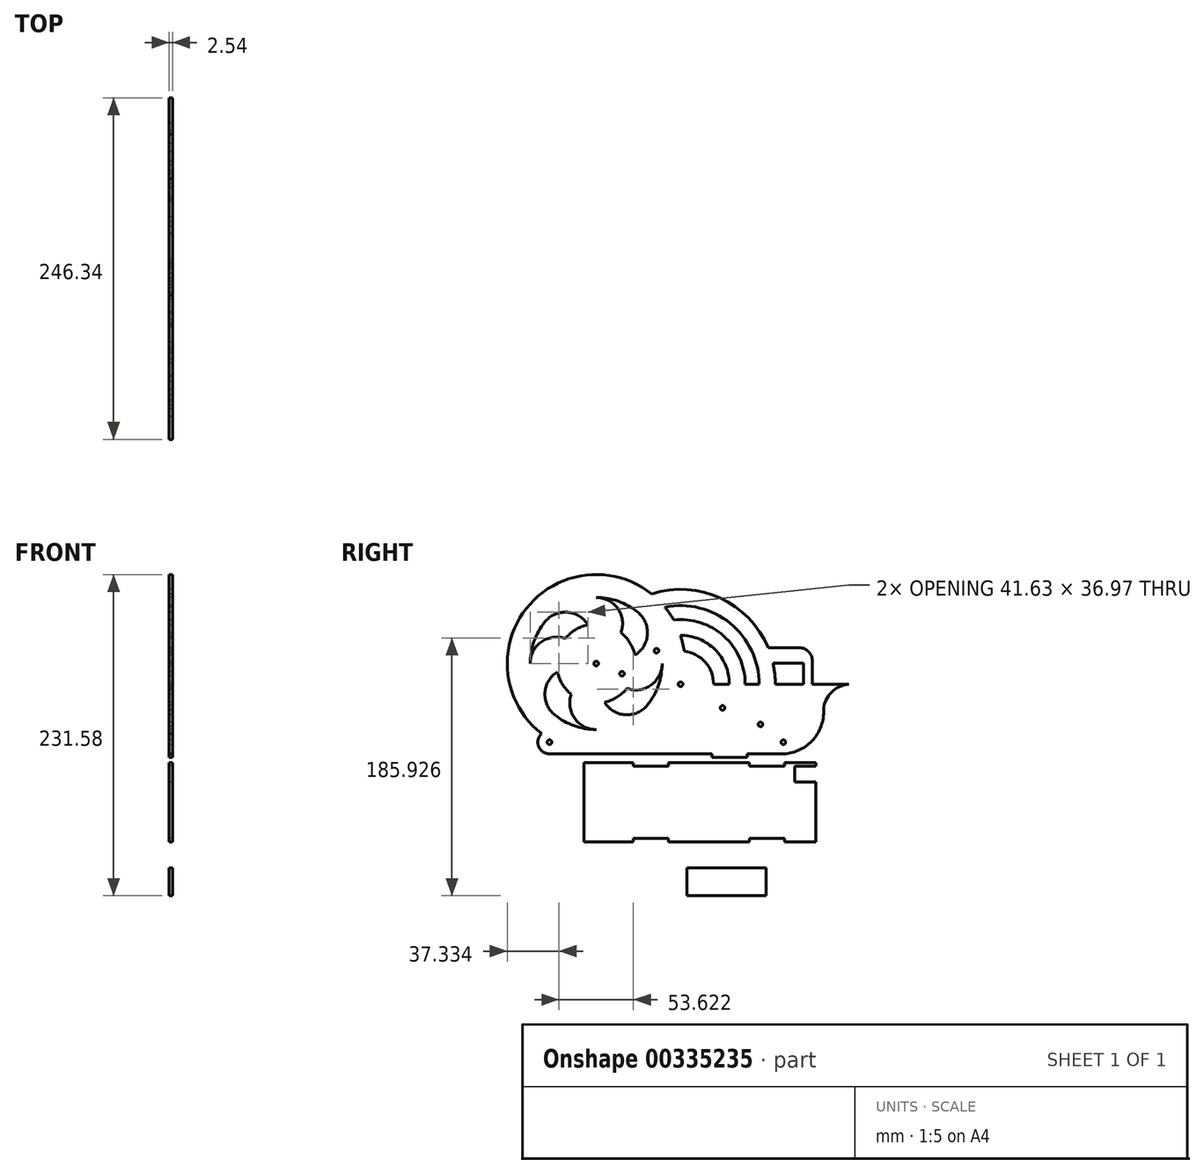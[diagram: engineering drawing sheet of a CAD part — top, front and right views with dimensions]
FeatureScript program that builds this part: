
annotation { "Feature Type Name" : "Feature", "Feature Type Description" : "" }
export const myFeature = defineFeature(function(context is Context, id is Id, definition is map)
    precondition{}
    {
        {
            var Q0;
            Q0=qCreatedBy(makeId("Right.planeOp"),FACE);
            var sketch = newSketch(context, id + "F0", { "sketchPlane" : qUnion([Q0])});
            skLineSegment(sketch, "E0.top", {"start": v(-77.01, -68.22) * mm, "end": v(57.1, -68.22) * mm});
            skArc(sketch, "E1", {"start": v(-113.69, 26.92) * mm, "mid": v(-121.55, 12.87) * mm, "end": v(-124.27, -3) * mm});
            skArc(sketch, "E2", {"start": v(-104.58, -9) * mm, "mid": v(-100.99, -17.98) * mm, "end": v(-94.6, -25.23) * mm});
            skArc(sketch, "E3", {"start": v(-48.7, 2.99) * mm, "mid": v(-39.67, 18) * mm, "end": v(-46.71, 34.03) * mm});
            skArc(sketch, "E4", {"start": v(-82.64, 24.93) * mm, "mid": v(-97.65, 33.96) * mm, "end": v(-113.69, 26.92) * mm});
            skArc(sketch, "E5.trimOffspring", {"start": v(-104.58, -9) * mm, "mid": v(-113.62, -24.01) * mm, "end": v(-106.58, -40.05) * mm});
            skArc(sketch, "E6.trimOffspring", {"start": v(-58.68, 19.22) * mm, "mid": v(-61.1, 36.56) * mm, "end": v(-76.65, 44.62) * mm});
            skArc(sketch, "E7.trimOffspring", {"start": v(-54.42, -20.97) * mm, "mid": v(-37.07, -18.56) * mm, "end": v(-29.02, -3) * mm});
            skArc(sketch, "E8.trimOffspring", {"start": v(-70.65, -30.95) * mm, "mid": v(-55.64, -39.98) * mm, "end": v(-39.6, -32.94) * mm});
            skArc(sketch, "E9.trimOffspring", {"start": v(-94.6, -25.23) * mm, "mid": v(-92.2, -42.58) * mm, "end": v(-76.65, -50.63) * mm});
            skArc(sketch, "E10.trimOffspring", {"start": v(-98.87, 14.95) * mm, "mid": v(-116.22, 12.54) * mm, "end": v(-124.27, -3) * mm});
            skArc(sketch, "E11.trimOffspring", {"start": v(-82.64, 24.93) * mm, "mid": v(-91.61, 21.33) * mm, "end": v(-98.87, 14.95) * mm});
            skArc(sketch, "E12.trimOffspring", {"start": v(-48.7, 2.99) * mm, "mid": v(-52.3, 11.96) * mm, "end": v(-58.68, 19.22) * mm});
            skArc(sketch, "E13.trimOffspring", {"start": v(-70.65, -30.95) * mm, "mid": v(-61.68, -27.35) * mm, "end": v(-54.42, -20.97) * mm});
            skArc(sketch, "E14.trimOffspring", {"start": v(-46.71, 34.03) * mm, "mid": v(-60.77, 41.9) * mm, "end": v(-76.65, 44.62) * mm});
            skArc(sketch, "E15.trimOffspring", {"start": v(-39.6, -32.94) * mm, "mid": v(-31.74, -18.88) * mm, "end": v(-29.02, -3) * mm});
            skArc(sketch, "E16.trimOffspring", {"start": v(-106.58, -40.05) * mm, "mid": v(-92.52, -47.91) * mm, "end": v(-76.65, -50.63) * mm});
            skArc(sketch, "E17", {"start": v(-116.08, -53.6) * mm, "mid": v(-118.2, -62.86) * mm, "end": v(-110.34, -68.22) * mm});
            skLineSegment(sketch, "E18", {"start": v(-77.01, -68.22) * mm, "end": v(-110.34, -68.22) * mm});
            skCircle(sketch, "E19", {"center": v(-76.65, -3) * mm, "radius": 1.65 * mm});
            skCircle(sketch, "E20", {"center": v(-110.34, -59.78) * mm, "radius": 1.65 * mm});
            skCircle(sketch, "E21", {"center": v(-58, -10.34) * mm, "radius": 1.65 * mm});
            skCircle(sketch, "E22", {"center": v(-33.13, 6.22) * mm, "radius": 1.65 * mm});
            skCircle(sketch, "E23", {"center": v(-15.73, -17.93) * mm, "radius": 1.65 * mm});
            skCircle(sketch, "E24", {"center": v(58.48, -59.78) * mm, "radius": 1.65 * mm});
            skLineSegment(sketch, "E25", {"start": v(-110.34, -59.78) * mm, "end": v(124.2, -59.78) * mm, "construction": true});
            skArc(sketch, "E26", {"start": v(105.55, -17.93) * mm, "mid": v(93.18, -23.78) * mm, "end": v(87.46, -36.2) * mm});
            skArc(sketch, "E27.trimOffspring", {"start": v(57.1, -68.22) * mm, "mid": v(79.18, -58.75) * mm, "end": v(87.46, -36.2) * mm});
            skLineSegment(sketch, "E28", {"start": v(105.55, -17.93) * mm, "end": v(79.3, -17.93) * mm});
            skPoint(sketch, "E29.orphan", {"position": v(-6.62, -17.93) * mm});
            skArc(sketch, "E30.trimOffspring", {"start": v(52.65, -17.93) * mm, "mid": v(52.23, -10.34) * mm, "end": v(50.97, -2.85) * mm});
            skLineSegment(sketch, "E31", {"start": v(47.42, 8.3) * mm, "end": v(70.21, 8.3) * mm});
            skLineSegment(sketch, "E32", {"start": v(79.3, -0.8) * mm, "end": v(79.3, -17.93) * mm});
            skLineSegment(sketch, "E33", {"start": v(50.97, -2.85) * mm, "end": v(72.84, -2.85) * mm});
            skLineSegment(sketch, "E34", {"start": v(72.84, -2.85) * mm, "end": v(72.84, -17.93) * mm});
            skArc(sketch, "E35", {"start": v(79.3, -0.8) * mm, "mid": v(76.64, 5.64) * mm, "end": v(70.21, 8.3) * mm});
            skArc(sketch, "E36.trimOffspring", {"start": v(47.42, 8.3) * mm, "mid": v(12.95, 44.14) * mm, "end": v(-36.68, 47.16) * mm});
            skLineSegment(sketch, "E37.trimOffspring", {"start": v(72.84, -17.93) * mm, "end": v(52.65, -17.93) * mm});
            skCircle(sketch, "E38", {"center": v(14.56, -35.01) * mm, "radius": 1.65 * mm});
            skCircle(sketch, "E39", {"center": v(41.94, -46.95) * mm, "radius": 1.65 * mm});
            skArc(sketch, "E40", {"start": v(-13.1, 5.78) * mm, "mid": v(-14.18, 11.58) * mm, "end": v(-15.8, 17.27) * mm});
            skArc(sketch, "E41", {"start": v(8.13, -17.93) * mm, "mid": v(2.04, -2.02) * mm, "end": v(-13.1, 5.78) * mm});
            skLineSegment(sketch, "E42", {"start": v(40.93, -17.93) * mm, "end": v(30.9, -17.93) * mm});
            skArc(sketch, "E43.trimOffspring", {"start": v(40.93, -17.93) * mm, "mid": v(20.13, 25.93) * mm, "end": v(-27, 37.6) * mm});
            skArc(sketch, "E44.trimOffspring", {"start": v(-36.68, 47.16) * mm, "mid": v(-127.02, 36.7) * mm, "end": v(-116.08, -53.6) * mm});
            skArc(sketch, "E45", {"start": v(30.9, -17.93) * mm, "mid": v(15.42, 16.76) * mm, "end": v(-20.73, 28.42) * mm});
            skArc(sketch, "E46", {"start": v(19.47, -17.93) * mm, "mid": v(9.14, 6.98) * mm, "end": v(-15.8, 17.27) * mm});
            skLineSegment(sketch, "E47.trimOffspring", {"start": v(19.47, -17.93) * mm, "end": v(8.13, -17.93) * mm});
            skArc(sketch, "E48.trimOffspring", {"start": v(-20.73, 28.42) * mm, "mid": v(-23.66, 33.14) * mm, "end": v(-27, 37.6) * mm});
            skLineSegment(sketch, "E49.bottom", {"start": v(-77.01, -68.22) * mm, "end": v(-51.61, -68.22) * mm});
            skLineSegment(sketch, "E49.top", {"start": v(-77.01, -70.76) * mm, "end": v(-51.61, -70.76) * mm});
            skLineSegment(sketch, "E49.left", {"start": v(-77.01, -68.22) * mm, "end": v(-77.01, -70.76) * mm});
            skLineSegment(sketch, "E49.right", {"start": v(-51.61, -68.22) * mm, "end": v(-51.61, -70.76) * mm});
            skLineSegment(sketch, "E50.bottom", {"start": v(32.38, -68.22) * mm, "end": v(57.78, -68.22) * mm});
            skLineSegment(sketch, "E51", {"start": v(-110.34, -86.16) * mm, "end": v(57.1, -86.16) * mm, "construction": true});
            skLineSegment(sketch, "E52", {"start": v(-110.34, -77.8) * mm, "end": v(-77.01, -77.8) * mm, "construction": true});
            skLineSegment(sketch, "E53.bottom", {"start": v(6.98, -70.76) * mm, "end": v(32.38, -70.76) * mm});
            skLineSegment(sketch, "E53.top", {"start": v(6.98, -68.22) * mm, "end": v(32.38, -68.22) * mm});
            skLineSegment(sketch, "E53.left", {"start": v(6.98, -70.76) * mm, "end": v(6.98, -68.22) * mm});
            skLineSegment(sketch, "E53.right", {"start": v(32.38, -70.76) * mm, "end": v(32.38, -68.22) * mm});
            skPoint(sketch, "E50.top.start.orphan", {"position": v(23.32, -70.76) * mm});
            skLineSegment(sketch, "E54", {"start": v(6.98, -77.7) * mm, "end": v(-51.61, -77.7) * mm, "construction": true});
            skSolve(sketch);
        }
        {
            var Q0;
            Q0=makeQuery(id+"F0.imprint","IMPRINT",FACE,{"disambiguationData":[TD([[makeQuery(id+"F0.imprint","IMPRINT",EDGE,{"derivedFrom":sQuery(id+"F0.wireOp",EDGE,"E1")}),-1.0]])]});
            var Q1;
            Q1=makeQuery(id+"F0.imprint","IMPRINT",FACE,{"disambiguationData":[TD([[makeQuery(id+"F0.imprint","IMPRINT",EDGE,{"derivedFrom":sQuery(id+"F0.wireOp",EDGE,"E0.right")}),-1.0]])]});
            var Q2;
            Q2=makeQuery(id+"F0.imprint","IMPRINT",FACE,{"disambiguationData":[TD([[makeQuery(id+"F0.imprint","IMPRINT",EDGE,{"derivedFrom":sQuery(id+"F0.wireOp",EDGE,"E49.bottom")}),-1.0]])]});
            var Q3;
            Q3=makeQuery(id+"F0.imprint","IMPRINT",FACE,{"disambiguationData":[TD([[makeQuery(id+"F0.imprint","IMPRINT",EDGE,{"derivedFrom":sQuery(id+"F0.wireOp",EDGE,"E50.bottom")}),-1.0]])]});
            var Q4;
            Q4=makeQuery(id+"F0.imprint","IMPRINT",FACE,{"disambiguationData":[TD([[makeQuery(id+"F0.imprint","IMPRINT",EDGE,{"derivedFrom":sQuery(id+"F0.wireOp",EDGE,"E53.bottom")}),1.0]])]});
            extrude(context, id + "F1", {"entities" : qUnion([Q0, Q1, Q2, Q3, Q4]), "depth" : 2.54 * mm});
        }
        {
            var Q0;
            Q0=qCreatedBy(makeId("Right.planeOp"),FACE);
            var sketch = newSketch(context, id + "F2", { "sketchPlane" : qUnion([Q0])});
            skLineSegment(sketch, "E55.bottom", {"start": v(-85.52, -74.5) * mm, "end": v(-50, -74.5) * mm});
            skLineSegment(sketch, "E55.left", {"start": v(-85.52, -74.5) * mm, "end": v(-85.52, -131.65) * mm});
            skLineSegment(sketch, "E55.right", {"start": v(81.92, -74.5) * mm, "end": v(81.92, -131.65) * mm});
            skLineSegment(sketch, "E56", {"start": v(-85.52, -77.04) * mm, "end": v(-50, -77.04) * mm, "construction": true});
            skLineSegment(sketch, "E57.top", {"start": v(-50, -77.04) * mm, "end": v(-24.6, -77.04) * mm});
            skLineSegment(sketch, "E57.left", {"start": v(-50, -74.5) * mm, "end": v(-50, -77.04) * mm});
            skLineSegment(sketch, "E57.right", {"start": v(-24.6, -74.5) * mm, "end": v(-24.6, -77.04) * mm});
            skLineSegment(sketch, "E58.bottom", {"start": v(33.98, -77.04) * mm, "end": v(59.38, -77.04) * mm});
            skLineSegment(sketch, "E58.left", {"start": v(33.98, -77.04) * mm, "end": v(33.98, -74.5) * mm});
            skLineSegment(sketch, "E58.right", {"start": v(59.38, -77.04) * mm, "end": v(59.38, -74.5) * mm});
            skLineSegment(sketch, "E59.trimOffspring", {"start": v(-24.6, -74.5) * mm, "end": v(33.98, -74.5) * mm});
            skLineSegment(sketch, "E60.trimOffspring", {"start": v(59.38, -74.5) * mm, "end": v(81.92, -74.5) * mm});
            skLineSegment(sketch, "E61", {"start": v(81.92, -131.65) * mm, "end": v(59.38, -131.65) * mm});
            skLineSegment(sketch, "E62.top", {"start": v(-50, -129.1) * mm, "end": v(-24.6, -129.1) * mm});
            skLineSegment(sketch, "E62.left", {"start": v(-50, -131.65) * mm, "end": v(-50, -129.1) * mm});
            skLineSegment(sketch, "E62.right", {"start": v(-24.6, -131.65) * mm, "end": v(-24.6, -129.1) * mm});
            skLineSegment(sketch, "E63.bottom", {"start": v(33.98, -129.1) * mm, "end": v(59.38, -129.1) * mm});
            skLineSegment(sketch, "E63.left", {"start": v(33.98, -129.1) * mm, "end": v(33.98, -131.65) * mm});
            skLineSegment(sketch, "E63.right", {"start": v(59.38, -129.1) * mm, "end": v(59.38, -131.65) * mm});
            skLineSegment(sketch, "E64.trimOffspring", {"start": v(33.98, -131.65) * mm, "end": v(-24.6, -131.65) * mm});
            skLineSegment(sketch, "E65.trimOffspring", {"start": v(-50, -131.65) * mm, "end": v(-85.52, -131.65) * mm});
            skLineSegment(sketch, "E66.bottom", {"start": v(81.92, -77.04) * mm, "end": v(66.68, -77.04) * mm});
            skLineSegment(sketch, "E66.top", {"start": v(81.92, -88.47) * mm, "end": v(66.68, -88.47) * mm});
            skLineSegment(sketch, "E66.left", {"start": v(81.92, -77.04) * mm, "end": v(81.92, -88.47) * mm});
            skLineSegment(sketch, "E66.right", {"start": v(66.68, -77.04) * mm, "end": v(66.68, -88.47) * mm});
            skLineSegment(sketch, "E67.bottom", {"start": v(-11.18, -150.26) * mm, "end": v(45.97, -150.26) * mm});
            skLineSegment(sketch, "E67.top", {"start": v(-11.18, -170.45) * mm, "end": v(45.97, -170.45) * mm});
            skLineSegment(sketch, "E67.left", {"start": v(-11.18, -150.26) * mm, "end": v(-11.18, -170.45) * mm});
            skLineSegment(sketch, "E67.right", {"start": v(45.97, -150.26) * mm, "end": v(45.97, -170.45) * mm});
            skSolve(sketch);
        }
        {
            var Q0;
            Q0=makeQuery(id+"F2.imprint","IMPRINT",FACE,{"disambiguationData":[TD([[makeQuery(id+"F2.imprint","IMPRINT",EDGE,{"derivedFrom":sQuery(id+"F2.wireOp",EDGE,"E55.bottom")}),-1.0]])]});
            var Q1;
            Q1=makeQuery(id+"F2.imprint","IMPRINT",FACE,{"disambiguationData":[TD([[makeQuery(id+"F2.imprint","IMPRINT",EDGE,{"derivedFrom":sQuery(id+"F2.wireOp",EDGE,"E67.bottom")}),-1.0]])]});
            extrude(context, id + "F3", {"entities" : qUnion([Q0, Q1]), "depth" : 2.54 * mm});
        }
    });
